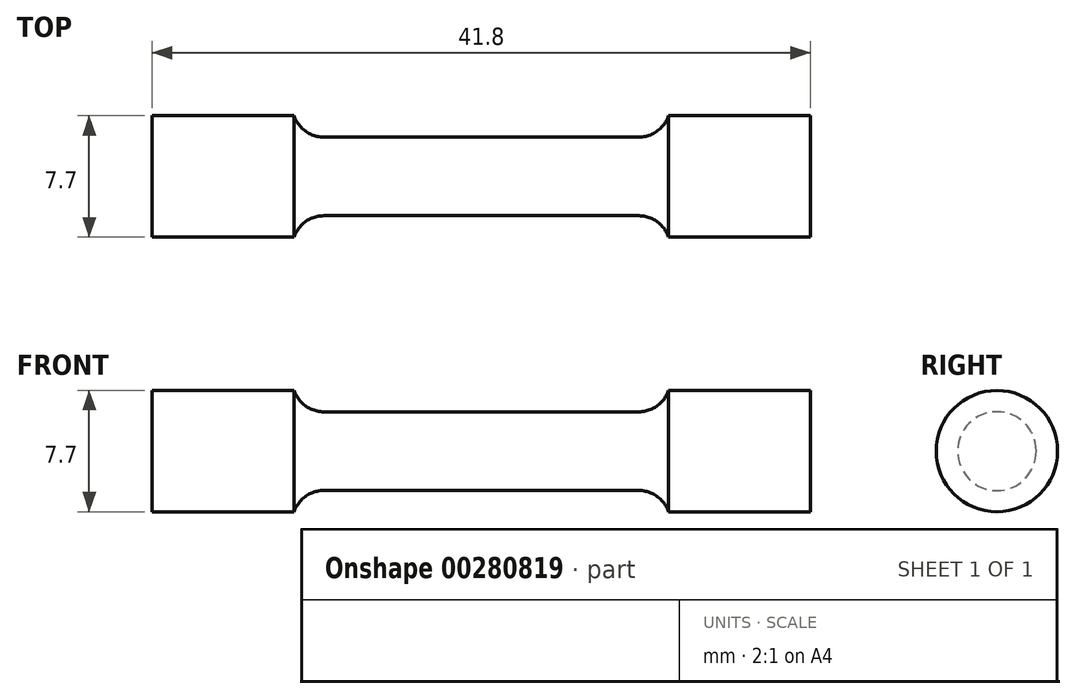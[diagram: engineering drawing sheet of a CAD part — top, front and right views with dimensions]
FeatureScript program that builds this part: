
annotation { "Feature Type Name" : "Feature", "Feature Type Description" : "" }
export const myFeature = defineFeature(function(context is Context, id is Id, definition is map)
    precondition{}
    {
        {
            var Q0;
            Q0=qCreatedBy(makeId("Front.planeOp"),FACE);
            var sketch = newSketch(context, id + "F0", { "sketchPlane" : qUnion([Q0])});
            skLineSegment(sketch, "E0", {"start": v(0, 2.5) * mm, "end": v(10, 2.5) * mm});
            skArc(sketch, "E1", {"start": v(10, 2.5) * mm, "mid": v(11.16, 2.87) * mm, "end": v(11.9, 3.85) * mm});
            skLineSegment(sketch, "E2", {"start": v(11.9, 3.85) * mm, "end": v(20.9, 3.85) * mm});
            skLineSegment(sketch, "E3", {"start": v(20.9, 3.85) * mm, "end": v(20.9, 0) * mm});
            skLineSegment(sketch, "E4.MirrorCS", {"start": v(0, 2.5) * mm, "end": v(-10, 2.5) * mm});
            skLineSegment(sketch, "E5.MirrorCS", {"start": v(-20.9, 3.85) * mm, "end": v(-20.9, 0) * mm});
            skLineSegment(sketch, "E6.MirrorCS", {"start": v(-11.9, 3.85) * mm, "end": v(-20.9, 3.85) * mm});
            skArc(sketch, "E7.MirrorCS", {"start": v(-10, 2.5) * mm, "mid": v(-11.16, 2.87) * mm, "end": v(-11.9, 3.85) * mm});
            skLineSegment(sketch, "E8", {"start": v(-20.9, 0) * mm, "end": v(20.9, 0) * mm});
            skSolve(sketch);
        }
        {
            var Q0;
            Q0 = qSketchRegion(id + "F0", true);
            var Q1;
            Q1=sQuery(id+"F0.wireOp",EDGE,"E8");
            revolve(context, id + "F1", {"entities" : qUnion([Q0]), "axis" : qUnion([Q1]), "revolveType" : RevolveType.FULL});
        }
    });
